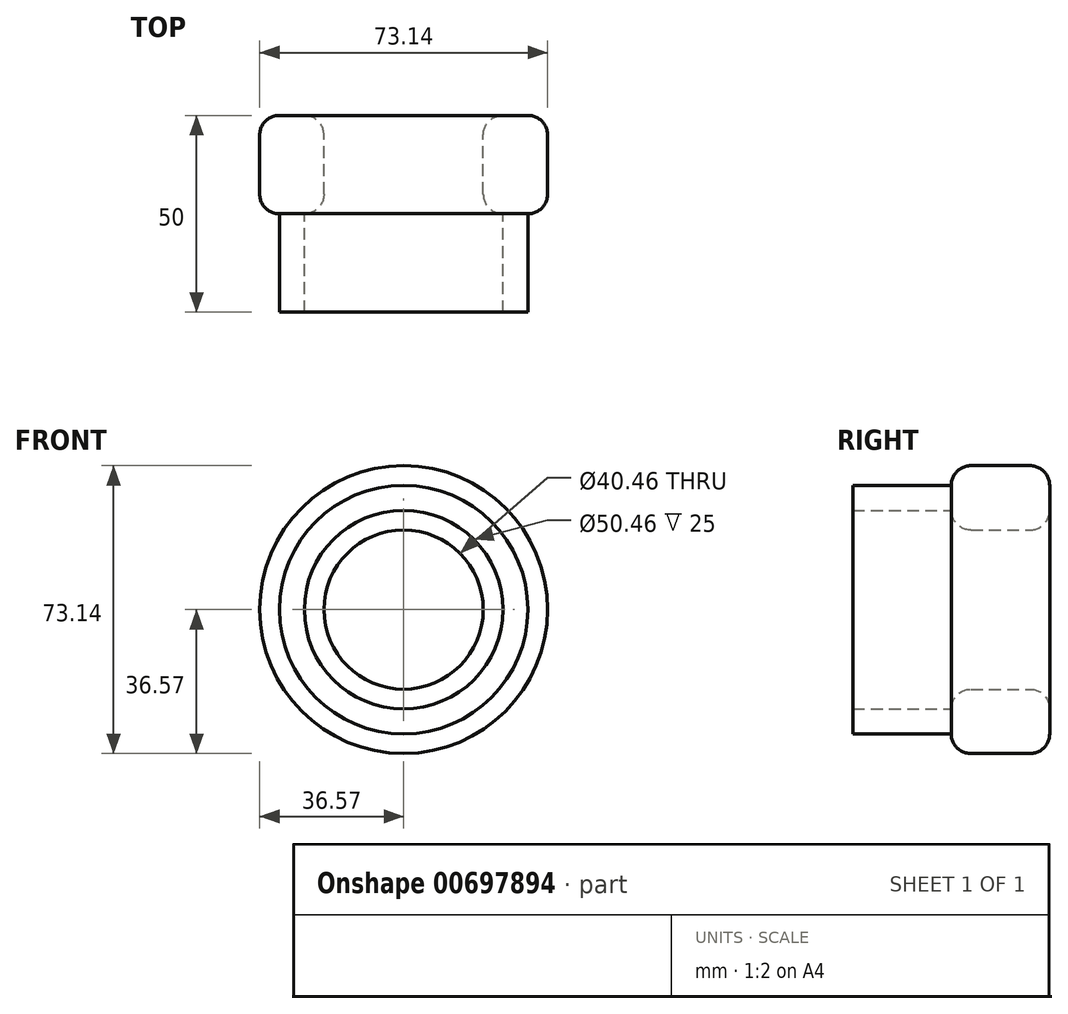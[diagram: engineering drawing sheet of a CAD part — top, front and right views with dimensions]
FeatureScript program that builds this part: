
annotation { "Feature Type Name" : "Feature", "Feature Type Description" : "" }
export const myFeature = defineFeature(function(context is Context, id is Id, definition is map)
    precondition{}
    {
        {
            var Q0;
            Q0=qCreatedBy(makeId("Front.planeOp"),FACE);
            var sketch = newSketch(context, id + "F0", { "sketchPlane" : qUnion([Q0])});
            skCircle(sketch, "E0", {"center": v(0, 0) * mm, "radius": 36.57 * mm});
            skCircle(sketch, "E1", {"center": v(0, 0) * mm, "radius": 20.23 * mm});
            skSolve(sketch);
        }
        {
            var Q0;
            Q0 = qSketchRegion(id + "F0", true);
            extrude(context, id + "F1", {"entities" : qUnion([Q0]), "depth" : 25 * mm, "offsetDistance" : 25 * mm});
        }
        {
            var Q0;
            Q0=makeQuery(id+"F1.opExtrude","CAP_EDGE",EDGE,{"disambiguationData":[OSD([sQuery(id+"F0.wireOp",EDGE,"E1")])],"isStart":false});
            fillet(context, id + "F2", {"entities" : qUnion([Q0]), "radius" : 5 * mm, "tangentPropagation" : true, "allowEdgeOverflow" : false});
        }
        {
            var Q0;
            Q0=makeQuery(id+"F1.opExtrude","CAP_EDGE",EDGE,{"disambiguationData":[OSD([sQuery(id+"F0.wireOp",EDGE,"E1")])],"isStart":true});
            fillet(context, id + "F3", {"entities" : qUnion([Q0]), "radius" : 5 * mm, "tangentPropagation" : true, "allowEdgeOverflow" : false});
        }
        {
            var Q0;
            Q0=makeQuery(id+"F1.opExtrude","CAP_EDGE",EDGE,{"disambiguationData":[OSD([sQuery(id+"F0.wireOp",EDGE,"E0")])],"isStart":true});
            fillet(context, id + "F4", {"entities" : qUnion([Q0]), "radius" : 5 * mm, "tangentPropagation" : true, "allowEdgeOverflow" : false});
        }
        {
            var Q0;
            Q0=makeQuery(id+"F1.opExtrude","CAP_EDGE",EDGE,{"disambiguationData":[OSD([sQuery(id+"F0.wireOp",EDGE,"E0")])],"isStart":false});
            fillet(context, id + "F5", {"entities" : qUnion([Q0]), "radius" : 5 * mm, "tangentPropagation" : true, "allowEdgeOverflow" : false});
        }
        {
            var Q0;
            Q0=makeQuery(id+"F1.opExtrude","CAP_FACE",FACE,{"disambiguationData":[OSD([sQuery(id+"F0.wireOp",EDGE,"E0"),sQuery(id+"F0.wireOp",EDGE,"E1")])],"isStart":false});
            extrude(context, id + "F6", {"entities" : qUnion([Q0]), "operationType" : NewBodyOperationType.ADD, "depth" : 25 * mm, "offsetDistance" : 25 * mm});
        }
    });
